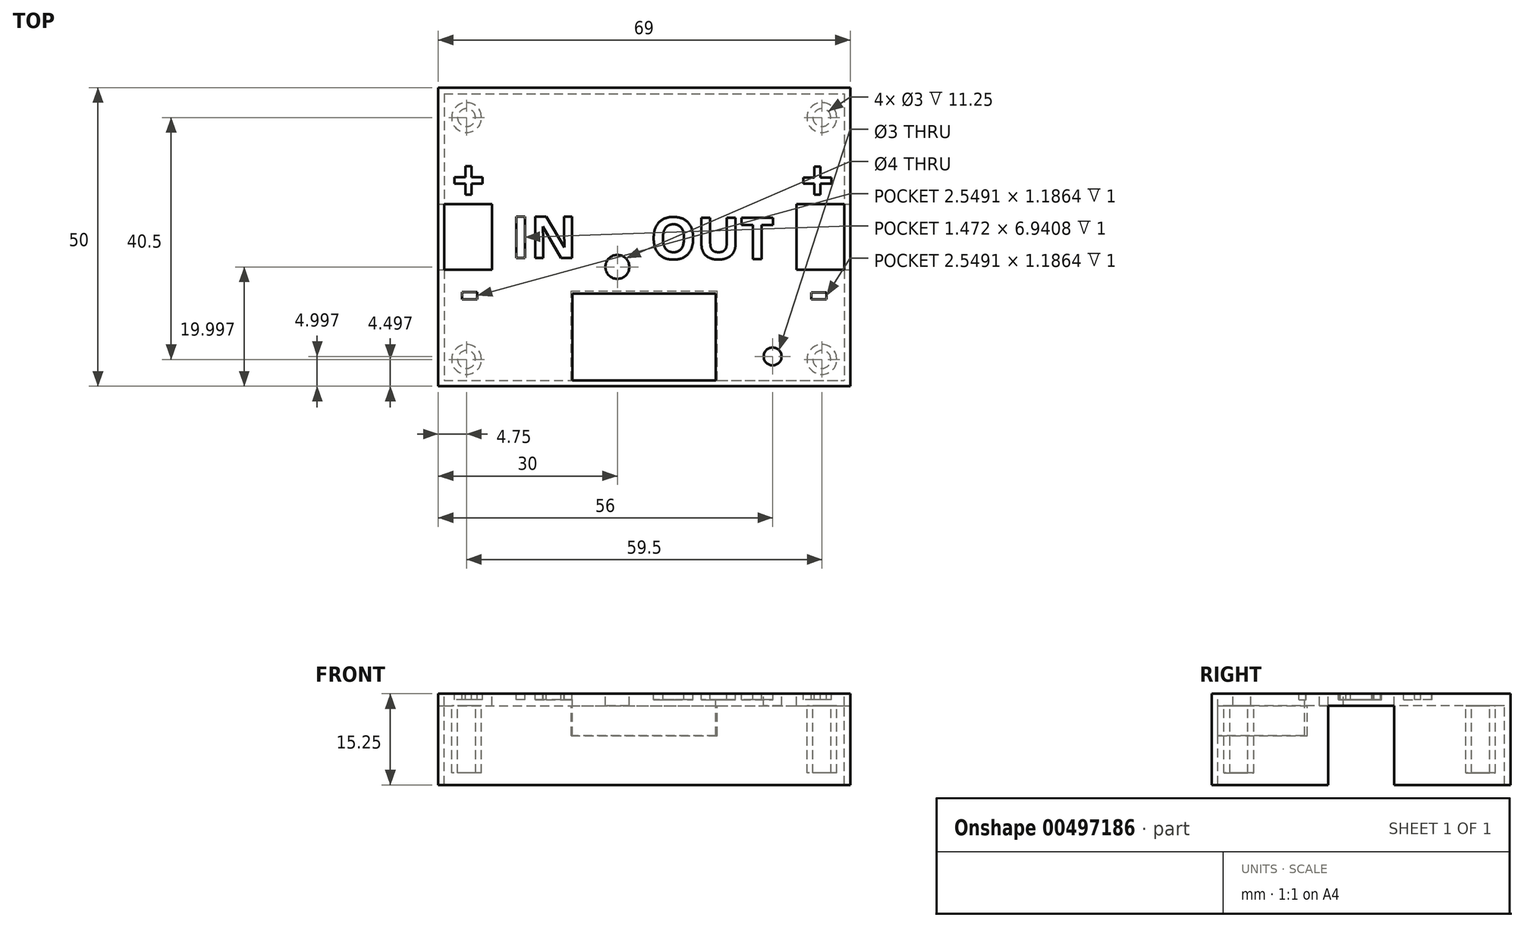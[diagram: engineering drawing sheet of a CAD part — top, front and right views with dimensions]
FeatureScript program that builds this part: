
annotation { "Feature Type Name" : "Feature", "Feature Type Description" : "" }
export const myFeature = defineFeature(function(context is Context, id is Id, definition is map)
    precondition{}
    {
        {
            var Q0;
            Q0=qCreatedBy(makeId("Top.planeOp"),FACE);
            var sketch = newSketch(context, id + "F0", { "sketchPlane" : qUnion([Q0])});
            skLineSegment(sketch, "E0.bottom", {"start": v(-33.5, 24.39) * mm, "end": v(33.5, 24.39) * mm});
            skLineSegment(sketch, "E0.top", {"start": v(-33.5, -23.61) * mm, "end": v(33.5, -23.61) * mm});
            skLineSegment(sketch, "E0.left", {"start": v(-33.5, 24.39) * mm, "end": v(-33.5, -23.61) * mm});
            skLineSegment(sketch, "E0.right", {"start": v(33.5, 24.39) * mm, "end": v(33.5, -23.61) * mm});
            skPoint(sketch, "E0.middle", {"position": v(0, 0.39) * mm});
            skLineSegment(sketch, "E1.bottom", {"start": v(-34.5, 25.39) * mm, "end": v(34.5, 25.39) * mm});
            skLineSegment(sketch, "E1.top", {"start": v(-34.5, -24.61) * mm, "end": v(34.5, -24.61) * mm});
            skLineSegment(sketch, "E1.left", {"start": v(-34.5, 25.39) * mm, "end": v(-34.5, -24.61) * mm});
            skLineSegment(sketch, "E1.right", {"start": v(34.5, 25.39) * mm, "end": v(34.5, -24.61) * mm});
            skPoint(sketch, "E2", {"position": v(-29.75, 20.39) * mm});
            skPoint(sketch, "E3", {"position": v(29.75, -20.11) * mm});
            skPoint(sketch, "E4", {"position": v(-29.75, -20.11) * mm});
            skCircle(sketch, "E5", {"center": v(-29.75, 20.39) * mm, "radius": 1.5 * mm});
            skCircle(sketch, "E6", {"center": v(-29.75, -20.11) * mm, "radius": 1.5 * mm});
            skCircle(sketch, "E7", {"center": v(29.75, -20.11) * mm, "radius": 1.5 * mm});
            skPoint(sketch, "E8", {"position": v(29.75, 20.39) * mm});
            skCircle(sketch, "E9", {"center": v(29.75, 20.39) * mm, "radius": 1.5 * mm});
            skCircle(sketch, "E10", {"center": v(-29.75, 20.39) * mm, "radius": 2.5 * mm});
            skCircle(sketch, "E11", {"center": v(29.75, 20.39) * mm, "radius": 2.5 * mm});
            skCircle(sketch, "E12", {"center": v(29.75, -20.11) * mm, "radius": 2.5 * mm});
            skCircle(sketch, "E13", {"center": v(-29.75, -20.11) * mm, "radius": 2.5 * mm});
            skPoint(sketch, "E14", {"position": v(33.5, 5.89) * mm});
            skPoint(sketch, "E15", {"position": v(-33.5, 5.89) * mm});
            skPoint(sketch, "E16", {"position": v(33.5, -5.11) * mm});
            skPoint(sketch, "E17", {"position": v(-33.5, -5.11) * mm});
            skPoint(sketch, "E18", {"position": v(25.5, 5.89) * mm});
            skPoint(sketch, "E19", {"position": v(25.5, -5.11) * mm});
            skPoint(sketch, "E20", {"position": v(-25.5, 5.89) * mm});
            skPoint(sketch, "E21", {"position": v(-25.5, -5.11) * mm});
            skPoint(sketch, "E22", {"position": v(12, -23.61) * mm});
            skPoint(sketch, "E23", {"position": v(12, -9.11) * mm});
            skPoint(sketch, "E24", {"position": v(-12, -23.61) * mm});
            skPoint(sketch, "E25", {"position": v(-12, -9.11) * mm});
            skLineSegment(sketch, "E26", {"start": v(-33.5, 5.89) * mm, "end": v(-25.5, 5.89) * mm});
            skLineSegment(sketch, "E27", {"start": v(-25.5, -5.11) * mm, "end": v(-25.5, 5.89) * mm});
            skLineSegment(sketch, "E28", {"start": v(-25.5, -5.11) * mm, "end": v(-33.5, -5.11) * mm});
            skLineSegment(sketch, "E29", {"start": v(25.5, 5.89) * mm, "end": v(25.5, -5.11) * mm});
            skLineSegment(sketch, "E30", {"start": v(25.5, -5.11) * mm, "end": v(33.5, -5.11) * mm});
            skLineSegment(sketch, "E31", {"start": v(25.5, 5.89) * mm, "end": v(33.5, 5.89) * mm});
            skLineSegment(sketch, "E32", {"start": v(12, -9.11) * mm, "end": v(-12, -9.11) * mm});
            skLineSegment(sketch, "E33", {"start": v(-12, -9.11) * mm, "end": v(-12, -23.61) * mm});
            skLineSegment(sketch, "E34", {"start": v(12, -9.11) * mm, "end": v(12, -23.61) * mm});
            skPoint(sketch, "E35", {"position": v(-4.5, -23.61) * mm});
            skPoint(sketch, "E36", {"position": v(-4.5, -4.61) * mm});
            skCircle(sketch, "E37", {"center": v(-4.5, -4.61) * mm, "radius": 2 * mm});
            skLineSegment(sketch, "E38", {"start": v(12, -9.11) * mm, "end": v(-12, -23.61) * mm, "construction": true});
            skLineSegment(sketch, "E39", {"start": v(-12, -9.11) * mm, "end": v(12, -23.61) * mm, "construction": true});
            skPoint(sketch, "E40", {"position": v(0, -16.36) * mm});
            skLineSegment(sketch, "E41.bottom", {"start": v(-12.25, -8.61) * mm, "end": v(12.25, -8.61) * mm});
            skPoint(sketch, "E42", {"position": v(21.5, -23.61) * mm});
            skPoint(sketch, "E43", {"position": v(21.5, -19.61) * mm});
            skCircle(sketch, "E44", {"center": v(21.5, -19.61) * mm, "radius": 1.5 * mm});
            skPoint(sketch, "E45", {"position": v(-12.25, -23.61) * mm});
            skPoint(sketch, "E46", {"position": v(12.25, -23.61) * mm});
            skLineSegment(sketch, "E47", {"start": v(-12.25, -23.61) * mm, "end": v(-12.25, -8.61) * mm});
            skLineSegment(sketch, "E48", {"start": v(12.25, -23.61) * mm, "end": v(12.25, -8.61) * mm});
            skSolve(sketch);
        }
        {
            var Q0;
            {var subQ5=sQuery(id+"F0.wireOp",EDGE,"E0.bottom");Q0=makeQuery(id+"F0.imprint","IMPRINT",FACE,{"disambiguationData":[TD([[makeQuery(id+"F0.imprint","IMPRINT",EDGE,{"derivedFrom":subQ5}),1.0]])]});}
            extrude(context, id + "F1", {"entities" : qUnion([Q0]), "oppositeDirection" : true, "depth" : 15.25 * mm, "offsetDistance" : 25 * mm});
        }
        {
            var Q0;
            {var subQ4=sQuery(id+"F0.wireOp",EDGE,"E0.bottom");Q0=makeQuery(id+"F0.imprint","IMPRINT",FACE,{"disambiguationData":[TD([[makeQuery(id+"F0.imprint","IMPRINT",EDGE,{"derivedFrom":subQ4}),-1.0]])]});}
            var Q1;
            Q1=makeQuery(id+"F0.imprint","IMPRINT",FACE,{"disambiguationData":[TD([[makeQuery(id+"F0.imprint","IMPRINT",EDGE,{"derivedFrom":sQuery(id+"F0.wireOp",EDGE,"E5")}),-1.0]])]});
            var Q2;
            Q2=makeQuery(id+"F0.imprint","IMPRINT",FACE,{"disambiguationData":[TD([[makeQuery(id+"F0.imprint","IMPRINT",EDGE,{"derivedFrom":sQuery(id+"F0.wireOp",EDGE,"E5")}),1.0]])]});
            var Q3;
            Q3=makeQuery(id+"F0.imprint","IMPRINT",FACE,{"disambiguationData":[TD([[makeQuery(id+"F0.imprint","IMPRINT",EDGE,{"derivedFrom":sQuery(id+"F0.wireOp",EDGE,"E9")}),1.0]])]});
            var Q4;
            Q4=makeQuery(id+"F0.imprint","IMPRINT",FACE,{"disambiguationData":[TD([[makeQuery(id+"F0.imprint","IMPRINT",EDGE,{"derivedFrom":sQuery(id+"F0.wireOp",EDGE,"E9")}),-1.0]])]});
            var Q5;
            Q5=makeQuery(id+"F0.imprint","IMPRINT",FACE,{"disambiguationData":[TD([[makeQuery(id+"F0.imprint","IMPRINT",EDGE,{"derivedFrom":sQuery(id+"F0.wireOp",EDGE,"E7")}),-1.0]])]});
            var Q6;
            Q6=makeQuery(id+"F0.imprint","IMPRINT",FACE,{"disambiguationData":[TD([[makeQuery(id+"F0.imprint","IMPRINT",EDGE,{"derivedFrom":sQuery(id+"F0.wireOp",EDGE,"E7")}),1.0]])]});
            var Q7;
            Q7=makeQuery(id+"F0.imprint","IMPRINT",FACE,{"disambiguationData":[TD([[makeQuery(id+"F0.imprint","IMPRINT",EDGE,{"derivedFrom":sQuery(id+"F0.wireOp",EDGE,"E6")}),-1.0]])]});
            var Q8;
            Q8=makeQuery(id+"F0.imprint","IMPRINT",FACE,{"disambiguationData":[TD([[makeQuery(id+"F0.imprint","IMPRINT",EDGE,{"derivedFrom":sQuery(id+"F0.wireOp",EDGE,"E6")}),1.0]])]});
            extrude(context, id + "F2", {"entities" : qUnion([Q0, Q1, Q2, Q3, Q4, Q5, Q6, Q7, Q8]), "operationType" : NewBodyOperationType.ADD, "oppositeDirection" : true, "depth" : 2 * mm, "offsetDistance" : 25 * mm});
        }
        {
            var Q0;
            Q0=makeQuery(id+"F0.imprint","IMPRINT",FACE,{"disambiguationData":[TD([[makeQuery(id+"F0.imprint","IMPRINT",EDGE,{"derivedFrom":sQuery(id+"F0.wireOp",EDGE,"E5")}),-1.0]])]});
            var Q1;
            Q1=makeQuery(id+"F0.imprint","IMPRINT",FACE,{"disambiguationData":[TD([[makeQuery(id+"F0.imprint","IMPRINT",EDGE,{"derivedFrom":sQuery(id+"F0.wireOp",EDGE,"E9")}),-1.0]])]});
            var Q2;
            Q2=makeQuery(id+"F0.imprint","IMPRINT",FACE,{"disambiguationData":[TD([[makeQuery(id+"F0.imprint","IMPRINT",EDGE,{"derivedFrom":sQuery(id+"F0.wireOp",EDGE,"E7")}),-1.0]])]});
            var Q3;
            Q3=makeQuery(id+"F0.imprint","IMPRINT",FACE,{"disambiguationData":[TD([[makeQuery(id+"F0.imprint","IMPRINT",EDGE,{"derivedFrom":sQuery(id+"F0.wireOp",EDGE,"E6")}),-1.0]])]});
            extrude(context, id + "F3", {"entities" : qUnion([Q0, Q1, Q2, Q3]), "operationType" : NewBodyOperationType.ADD, "oppositeDirection" : true, "depth" : 13.25 * mm, "offsetDistance" : 25 * mm});
        }
        {
            var Q0;
            Q0=makeQuery(id+"F1.opExtrude","SWEPT_FACE",FACE,{"disambiguationData":[OSD([sQuery(id+"F0.wireOp",EDGE,"E1.right")])]});
            var sketch = newSketch(context, id + "F4", { "sketchPlane" : qUnion([Q0])});
            skPoint(sketch, "E49", {"position": v(-5.11, -15.25) * mm});
            skPoint(sketch, "E50", {"position": v(5.89, -15.25) * mm});
            skPoint(sketch, "E51", {"position": v(5.89, -2) * mm});
            skPoint(sketch, "E52", {"position": v(-5.11, -2) * mm});
            skLineSegment(sketch, "E53", {"start": v(-5.11, -15.25) * mm, "end": v(-5.11, -2) * mm});
            skLineSegment(sketch, "E54", {"start": v(-5.11, -2) * mm, "end": v(5.89, -2) * mm});
            skLineSegment(sketch, "E55", {"start": v(5.89, -2) * mm, "end": v(5.89, -15.25) * mm});
            skLineSegment(sketch, "E56", {"start": v(5.89, -15.25) * mm, "end": v(-5.11, -15.25) * mm});
            skSolve(sketch);
        }
        {
            var Q0;
            Q0=makeQuery(id+"F4.imprint","IMPRINT",FACE,{"disambiguationData":[TD([[makeQuery(id+"F4.imprint","IMPRINT",EDGE,{"derivedFrom":sQuery(id+"F4.wireOp",EDGE,"E53")}),-1.0]])]});
            extrude(context, id + "F5", {"entities" : qUnion([Q0]), "operationType" : NewBodyOperationType.REMOVE, "oppositeDirection" : true, "depth" : 75 * mm, "offsetDistance" : 25 * mm});
        }
        {
            var Q0;
            Q0=makeQuery(id+"F0.imprint","IMPRINT",FACE,{"disambiguationData":[TD([[makeQuery(id+"F0.imprint","IMPRINT",EDGE,{"derivedFrom":sQuery(id+"F0.wireOp",EDGE,"E32")}),-1.0]])]});
            var Q1;
            {var subQ0=sQuery(id+"F0.wireOp",EDGE,"E41.top");Q1=makeQuery(id+"F0.imprint","IMPRINT",FACE,{"disambiguationData":[TD([[makeQuery(id+"F0.imprint","IMPRINT",EDGE,{"derivedFrom":subQ0}),1.0]])]});}
            extrude(context, id + "F6", {"entities" : qUnion([Q0, Q1]), "oppositeDirection" : true, "depth" : 7 * mm, "offsetDistance" : 25 * mm});
        }
        {
            var Q0;
            Q0=makeQuery(id+"F1.opExtrude","SWEPT_BODY",BODY,{"disambiguationData":[OSD([sQuery(id+"F0.wireOp",EDGE,"E0.bottom"),sQuery(id+"F0.wireOp",EDGE,"E0.top"),sQuery(id+"F0.wireOp",EDGE,"E0.left"),sQuery(id+"F0.wireOp",EDGE,"E0.right"),sQuery(id+"F0.wireOp",EDGE,"E1.bottom"),sQuery(id+"F0.wireOp",EDGE,"E1.top"),sQuery(id+"F0.wireOp",EDGE,"E1.left"),sQuery(id+"F0.wireOp",EDGE,"E1.right"),sQuery(id+"F0.wireOp",EDGE,"E41.top"),sQuery(id+"F0.wireOp",EDGE,"E41.left"),sQuery(id+"F0.wireOp",EDGE,"E41.right")])]});
            var Q1;
            Q1=makeQuery(id+"F6.opExtrude","SWEPT_BODY",BODY,{"disambiguationData":[OSD([sQuery(id+"F0.wireOp",EDGE,"E0.top"),sQuery(id+"F0.wireOp",EDGE,"E32"),sQuery(id+"F0.wireOp",EDGE,"E33"),sQuery(id+"F0.wireOp",EDGE,"E34"),sQuery(id+"F0.wireOp",EDGE,"E41.bottom"),sQuery(id+"F0.wireOp",EDGE,"E41.top"),sQuery(id+"F0.wireOp",EDGE,"E41.left"),sQuery(id+"F0.wireOp",EDGE,"E41.right")])]});
            booleanBodies(context, id + "F7", {"operationType" : BooleanOperationType.UNION, "tools" : qUnion([Q0, Q1])});
        }
        {
            var Q0;
            {var subQ0=sQuery(id+"F0.wireOp",EDGE,"E41.right");var subQ1=sQuery(id+"F0.wireOp",EDGE,"E41.left");var subQ2=sQuery(id+"F0.wireOp",EDGE,"E41.top");var subQ3=sQuery(id+"F0.wireOp",EDGE,"E41.bottom");var subQ4=sQuery(id+"F0.wireOp",EDGE,"E0.top");var subQ5=sQuery(id+"F0.wireOp",EDGE,"E0.right");var subQ6=sQuery(id+"F0.wireOp",EDGE,"E0.left");var subQ7=sQuery(id+"F0.wireOp",EDGE,"E0.bottom");Q0=makeQuery(id+"F7.opBoolean","MERGE",FACE,{"derivedFrom":[makeQuery(id+"F2.boolean.opBoolean","MERGE",FACE,{"derivedFrom":[makeQuery(id+"F1.opExtrude","CAP_FACE",FACE,{"disambiguationData":[OSD([subQ7,subQ4,subQ6,subQ5,sQuery(id+"F0.wireOp",EDGE,"E1.bottom"),sQuery(id+"F0.wireOp",EDGE,"E1.top"),sQuery(id+"F0.wireOp",EDGE,"E1.left"),sQuery(id+"F0.wireOp",EDGE,"E1.right"),subQ2,subQ1,subQ0])],"isStart":true}),makeQuery(id+"F2.opExtrude","CAP_FACE",FACE,{"disambiguationData":[OSD([subQ7,subQ4,subQ6,subQ5,sQuery(id+"F0.wireOp",EDGE,"E26"),sQuery(id+"F0.wireOp",EDGE,"E27"),sQuery(id+"F0.wireOp",EDGE,"E28"),sQuery(id+"F0.wireOp",EDGE,"E29"),sQuery(id+"F0.wireOp",EDGE,"E30"),sQuery(id+"F0.wireOp",EDGE,"E31"),sQuery(id+"F0.wireOp",EDGE,"E37"),subQ3,subQ1,subQ0])],"isStart":true})]}),makeQuery(id+"F6.opExtrude","CAP_FACE",FACE,{"disambiguationData":[OSD([subQ4,sQuery(id+"F0.wireOp",EDGE,"E32"),sQuery(id+"F0.wireOp",EDGE,"E33"),sQuery(id+"F0.wireOp",EDGE,"E34"),subQ3,subQ2,subQ1,subQ0])],"isStart":true})]});}
            var sketch = newSketch(context, id + "F8", { "sketchPlane" : qUnion([Q0])});
            skPoint(sketch, "E57", {"position": v(-22.33, -3.11) * mm});
            skPoint(sketch, "E58", {"position": v(-22.33, 3.89) * mm});
            skText(sketch, "E59", { "text": "IN", "fontName": "OpenSans-Bold.ttf"});
            skPoint(sketch, "E60", {"position": v(-22.5, 0.39) * mm});
            skPoint(sketch, "E60.positionSnap0", {"position": v(-25.5, 0.39) * mm});
            skPoint(sketch, "E61", {"position": v(22.5, 0) * mm});
            skPoint(sketch, "E62", {"position": v(1.02, -3.3) * mm});
            skPoint(sketch, "E63", {"position": v(1.02, 3.7) * mm});
            skText(sketch, "E64", { "text": "OUT", "fontName": "OpenSans-Bold.ttf"});
            skPoint(sketch, "E65", {"position": v(26.22, 6.41) * mm});
            skPoint(sketch, "E66", {"position": v(26.22, 13.41) * mm});
            skText(sketch, "E67", { "text": "+", "fontName": "OpenSans-Bold.ttf"});
            skPoint(sketch, "E68", {"position": v(29.5, 8.89) * mm});
            skPoint(sketch, "E68.positionSnap0", {"position": v(29.5, 5.89) * mm});
            skPoint(sketch, "E69", {"position": v(-29.5, 8.89) * mm});
            skPoint(sketch, "E69.positionSnap0", {"position": v(-29.5, 5.89) * mm});
            skPoint(sketch, "E70", {"position": v(-32.22, 6.43) * mm});
            skPoint(sketch, "E71", {"position": v(-26.46, 13.43) * mm});
            skText(sketch, "E72", { "text": "+", "fontName": "OpenSans-Bold.ttf"});
            skPoint(sketch, "E73", {"position": v(-29.5, -8.11) * mm});
            skPoint(sketch, "E73.positionSnap0", {"position": v(-29.5, -5.11) * mm});
            skPoint(sketch, "E74", {"position": v(29.5, -8.11) * mm});
            skPoint(sketch, "E74.positionSnap0", {"position": v(29.5, -5.11) * mm});
            skPoint(sketch, "E75", {"position": v(-30.8, -12.04) * mm});
            skPoint(sketch, "E76", {"position": v(-30.8, -5.04) * mm});
            skText(sketch, "E77", { "text": "-", "fontName": "OpenSans-Bold.ttf"});
            skPoint(sketch, "E78", {"position": v(27.7, -12.07) * mm});
            skPoint(sketch, "E79", {"position": v(-57.28, -5.07) * mm});
            skText(sketch, "E80", { "text": "-", "fontName": "OpenSans-Bold.ttf"});
            const initialGuessF8  = {"E59": [-0.02233, -0.00311, 1, 0, 0.007], "E64": [0.00102, -0.0033, 1, 0, 0.007], "E67": [0.02622, 0.00641, 1, 0, 0.007], "E72": [-0.03222, 0.00643, 1, 0, 0.007], "E77": [-0.0308, -0.01204, 1, 0, 0.007], "E80": [0.0277, -0.01207, 1, 0, 0.007]};
            skSetInitialGuess(sketch, initialGuessF8);
            skSolve(sketch);
        }
        {
            var Q0;
            Q0=makeQuery(id+"F8.imprint","IMPRINT",FACE,{"disambiguationData":[TD([[makeQuery(id+"F8.imprint","IMPRINT",EDGE,{"derivedFrom":sQuery(id+"F8.wireOp",EDGE,"E72.sketch_text.stroke-0")}),-1.0]])]});
            var Q1;
            Q1=makeQuery(id+"F8.imprint","IMPRINT",FACE,{"disambiguationData":[TD([[makeQuery(id+"F8.imprint","IMPRINT",EDGE,{"derivedFrom":sQuery(id+"F8.wireOp",EDGE,"E77.sketch_text.stroke-0")}),-1.0]])]});
            var Q2;
            Q2=makeQuery(id+"F8.imprint","IMPRINT",FACE,{"disambiguationData":[TD([[makeQuery(id+"F8.imprint","IMPRINT",EDGE,{"derivedFrom":sQuery(id+"F8.wireOp",EDGE,"E59.sketch_text.stroke-0")}),-1.0]])]});
            var Q3;
            Q3=makeQuery(id+"F8.imprint","IMPRINT",FACE,{"disambiguationData":[TD([[makeQuery(id+"F8.imprint","IMPRINT",EDGE,{"derivedFrom":sQuery(id+"F8.wireOp",EDGE,"E59.sketch_text.stroke-4")}),-1.0]])]});
            var Q4;
            Q4=makeQuery(id+"F8.imprint","IMPRINT",FACE,{"disambiguationData":[TD([[makeQuery(id+"F8.imprint","IMPRINT",EDGE,{"derivedFrom":sQuery(id+"F8.wireOp",EDGE,"E64.sketch_text.stroke-0")}),-1.0]])]});
            var Q5;
            Q5=makeQuery(id+"F8.imprint","IMPRINT",FACE,{"disambiguationData":[TD([[makeQuery(id+"F8.imprint","IMPRINT",EDGE,{"derivedFrom":sQuery(id+"F8.wireOp",EDGE,"E64.sketch_text.stroke-14")}),-1.0]])]});
            var Q6;
            Q6=makeQuery(id+"F8.imprint","IMPRINT",FACE,{"disambiguationData":[TD([[makeQuery(id+"F8.imprint","IMPRINT",EDGE,{"derivedFrom":sQuery(id+"F8.wireOp",EDGE,"E64.sketch_text.stroke-29")}),-1.0]])]});
            var Q7;
            Q7=makeQuery(id+"F8.imprint","IMPRINT",FACE,{"disambiguationData":[TD([[makeQuery(id+"F8.imprint","IMPRINT",EDGE,{"derivedFrom":sQuery(id+"F8.wireOp",EDGE,"E67.sketch_text.stroke-0")}),-1.0]])]});
            var Q8;
            Q8=makeQuery(id+"F8.imprint","IMPRINT",FACE,{"disambiguationData":[TD([[makeQuery(id+"F8.imprint","IMPRINT",EDGE,{"derivedFrom":sQuery(id+"F8.wireOp",EDGE,"E80.sketch_text.stroke-0")}),-1.0]])]});
            var Q9;
            Q9=makeQuery(id+"F8.imprint","IMPRINT",FACE,{"disambiguationData":[TD([[makeQuery(id+"F8.imprint","IMPRINT",EDGE,{"derivedFrom":sQuery(id+"F8.wireOp",EDGE,"de6e2c7f-5ea9-4b41-9146-05171a86de11.sketch_text.stroke-0")}),-1.0]])]});
            var Q10;
            Q10=makeQuery(id+"F8.imprint","IMPRINT",FACE,{"disambiguationData":[TD([[makeQuery(id+"F8.imprint","IMPRINT",EDGE,{"derivedFrom":sQuery(id+"F8.wireOp",EDGE,"de6e2c7f-5ea9-4b41-9146-05171a86de11.sketch_text.stroke-12")}),-1.0]])]});
            var Q11;
            Q11=makeQuery(id+"F8.imprint","IMPRINT",FACE,{"disambiguationData":[TD([[makeQuery(id+"F8.imprint","IMPRINT",EDGE,{"derivedFrom":sQuery(id+"F8.wireOp",EDGE,"de6e2c7f-5ea9-4b41-9146-05171a86de11.sketch_text.stroke-35")}),-1.0]])]});
            var Q12;
            Q12=makeQuery(id+"F8.imprint","IMPRINT",FACE,{"disambiguationData":[TD([[makeQuery(id+"F8.imprint","IMPRINT",EDGE,{"derivedFrom":sQuery(id+"F8.wireOp",EDGE,"de6e2c7f-5ea9-4b41-9146-05171a86de11.sketch_text.stroke-45")}),-1.0]])]});
            var Q13;
            Q13=makeQuery(id+"F8.imprint","IMPRINT",FACE,{"disambiguationData":[TD([[makeQuery(id+"F8.imprint","IMPRINT",EDGE,{"derivedFrom":sQuery(id+"F8.wireOp",EDGE,"de6e2c7f-5ea9-4b41-9146-05171a86de11.sketch_text.stroke-50")}),-1.0]])]});
            var Q14;
            Q14=makeQuery(id+"F8.imprint","IMPRINT",FACE,{"disambiguationData":[TD([[makeQuery(id+"F8.imprint","IMPRINT",EDGE,{"derivedFrom":sQuery(id+"F8.wireOp",EDGE,"de6e2c7f-5ea9-4b41-9146-05171a86de11.sketch_text.stroke-58")}),-1.0]])]});
            var Q15;
            Q15=makeQuery(id+"F8.imprint","IMPRINT",FACE,{"disambiguationData":[TD([[makeQuery(id+"F8.imprint","IMPRINT",EDGE,{"derivedFrom":sQuery(id+"F8.wireOp",EDGE,"de6e2c7f-5ea9-4b41-9146-05171a86de11.sketch_text.stroke-68")}),-1.0]])]});
            var Q16;
            Q16=makeQuery(id+"F8.imprint","IMPRINT",FACE,{"disambiguationData":[TD([[makeQuery(id+"F8.imprint","IMPRINT",EDGE,{"derivedFrom":sQuery(id+"F8.wireOp",EDGE,"de6e2c7f-5ea9-4b41-9146-05171a86de11.sketch_text.stroke-72")}),-1.0]])]});
            var Q17;
            Q17=makeQuery(id+"F8.imprint","IMPRINT",FACE,{"disambiguationData":[TD([[makeQuery(id+"F8.imprint","IMPRINT",EDGE,{"derivedFrom":sQuery(id+"F8.wireOp",EDGE,"de6e2c7f-5ea9-4b41-9146-05171a86de11.sketch_text.stroke-86")}),-1.0]])]});
            var Q18;
            Q18=makeQuery(id+"F8.imprint","IMPRINT",FACE,{"disambiguationData":[TD([[makeQuery(id+"F8.imprint","IMPRINT",EDGE,{"derivedFrom":sQuery(id+"F8.wireOp",EDGE,"de6e2c7f-5ea9-4b41-9146-05171a86de11.sketch_text.stroke-103")}),-1.0]])]});
            var Q19;
            Q19=makeQuery(id+"F8.imprint","IMPRINT",FACE,{"disambiguationData":[TD([[makeQuery(id+"F8.imprint","IMPRINT",EDGE,{"derivedFrom":sQuery(id+"F8.wireOp",EDGE,"dfe367e2-f470-4ccf-86bf-3b77ab677cfb.sketch_text.stroke-0")}),-1.0]])]});
            var Q20;
            Q20=makeQuery(id+"F8.imprint","IMPRINT",FACE,{"disambiguationData":[TD([[makeQuery(id+"F8.imprint","IMPRINT",EDGE,{"derivedFrom":sQuery(id+"F8.wireOp",EDGE,"dfe367e2-f470-4ccf-86bf-3b77ab677cfb.sketch_text.stroke-10")}),-1.0]])]});
            var Q21;
            Q21=makeQuery(id+"F8.imprint","IMPRINT",FACE,{"disambiguationData":[TD([[makeQuery(id+"F8.imprint","IMPRINT",EDGE,{"derivedFrom":sQuery(id+"F8.wireOp",EDGE,"dfe367e2-f470-4ccf-86bf-3b77ab677cfb.sketch_text.stroke-14")}),-1.0]])]});
            var Q22;
            Q22=makeQuery(id+"F8.imprint","IMPRINT",FACE,{"disambiguationData":[TD([[makeQuery(id+"F8.imprint","IMPRINT",EDGE,{"derivedFrom":sQuery(id+"F8.wireOp",EDGE,"dfe367e2-f470-4ccf-86bf-3b77ab677cfb.sketch_text.stroke-42")}),-1.0]])]});
            var Q23;
            Q23=makeQuery(id+"F8.imprint","IMPRINT",FACE,{"disambiguationData":[TD([[makeQuery(id+"F8.imprint","IMPRINT",EDGE,{"derivedFrom":sQuery(id+"F8.wireOp",EDGE,"dfe367e2-f470-4ccf-86bf-3b77ab677cfb.sketch_text.stroke-62")}),-1.0]])]});
            var Q24;
            Q24=makeQuery(id+"F8.imprint","IMPRINT",FACE,{"disambiguationData":[TD([[makeQuery(id+"F8.imprint","IMPRINT",EDGE,{"derivedFrom":sQuery(id+"F8.wireOp",EDGE,"dfe367e2-f470-4ccf-86bf-3b77ab677cfb.sketch_text.stroke-66")}),-1.0]])]});
            var Q25;
            Q25=makeQuery(id+"F8.imprint","IMPRINT",FACE,{"disambiguationData":[TD([[makeQuery(id+"F8.imprint","IMPRINT",EDGE,{"derivedFrom":sQuery(id+"F8.wireOp",EDGE,"dfe367e2-f470-4ccf-86bf-3b77ab677cfb.sketch_text.stroke-86")}),-1.0]])]});
            var Q26;
            Q26=makeQuery(id+"F8.imprint","IMPRINT",FACE,{"disambiguationData":[TD([[makeQuery(id+"F8.imprint","IMPRINT",EDGE,{"derivedFrom":sQuery(id+"F8.wireOp",EDGE,"dfe367e2-f470-4ccf-86bf-3b77ab677cfb.sketch_text.stroke-100")}),-1.0]])]});
            extrude(context, id + "F9", {"entities" : qUnion([Q0, Q1, Q2, Q3, Q4, Q5, Q6, Q7, Q8, Q9, Q10, Q11, Q12, Q13, Q14, Q15, Q16, Q17, Q18, Q19, Q20, Q21, Q22, Q23, Q24, Q25, Q26]), "operationType" : NewBodyOperationType.REMOVE, "oppositeDirection" : true, "depth" : 1 * mm, "offsetDistance" : 25 * mm});
        }
    });
